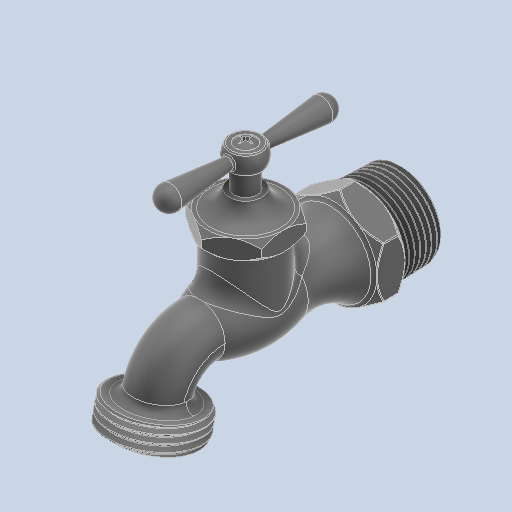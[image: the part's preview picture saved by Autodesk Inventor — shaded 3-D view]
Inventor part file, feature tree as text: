
AUTODESK INVENTOR PART (.ipt)
format: ipt  version: 2022 (Build 260153000, 153)  size: 1,861,632 bytes
history: native  units: in
note: dims shown in document units (in); Inventor stores cm internally (conversion verified against a paired STEP export)
features: revolve x3, other x3, boolean_combine x1, fillet x1
ambient origin geometry x8: Origin, YZ Plane, XZ Plane, XY Plane, X Axis, Y Axis, Z Axis, Center Point
bodies: Solid1 (feature_tree), Solid2 (feature_tree), Solid3 (feature_tree), Solid4 (feature_tree), Solid5 (feature_tree), Solid6 (feature_tree), Solid7 (feature_tree), Solid8 (feature_tree)
feature tree (8):
  revolve  "Revolve1[2]"  [1 undecoded]
  revolve  "Revolve1[4]"  [1 undecoded]
  revolve  "Revolve1[7]"  [1 undecoded]
  boolean_combine  "Combine1"
  fillet  "Fillet1"  [1 undecoded]
  other  "Cut-Extrude5"
  other  "Cut-Sweep2"
  other  "Cut-Extrude6[1]"
note: 4 required parameter values undecoded (feature->parameter linkage not recoverable at this tier; creation-order binding heuristic only, values carry confidence <= 0.55)
